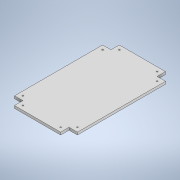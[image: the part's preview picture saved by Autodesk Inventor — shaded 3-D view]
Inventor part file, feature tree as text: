
AUTODESK INVENTOR PART (.ipt)
format: ipt  version: 2020 (Build 240168000, 168)  size: 127,488 bytes
history: native  units: mm
features: extrude x1, sketch x1
ambient origin geometry x8: Origin, YZ Plane, XZ Plane, XY Plane, X Axis, Y Axis, Z Axis, Center Point
bodies: Solide1 (feature_tree)
feature tree (2):
  extrude  "Extrusion1"  Depth=150.0mm
  sketch  "Esquisse1"
